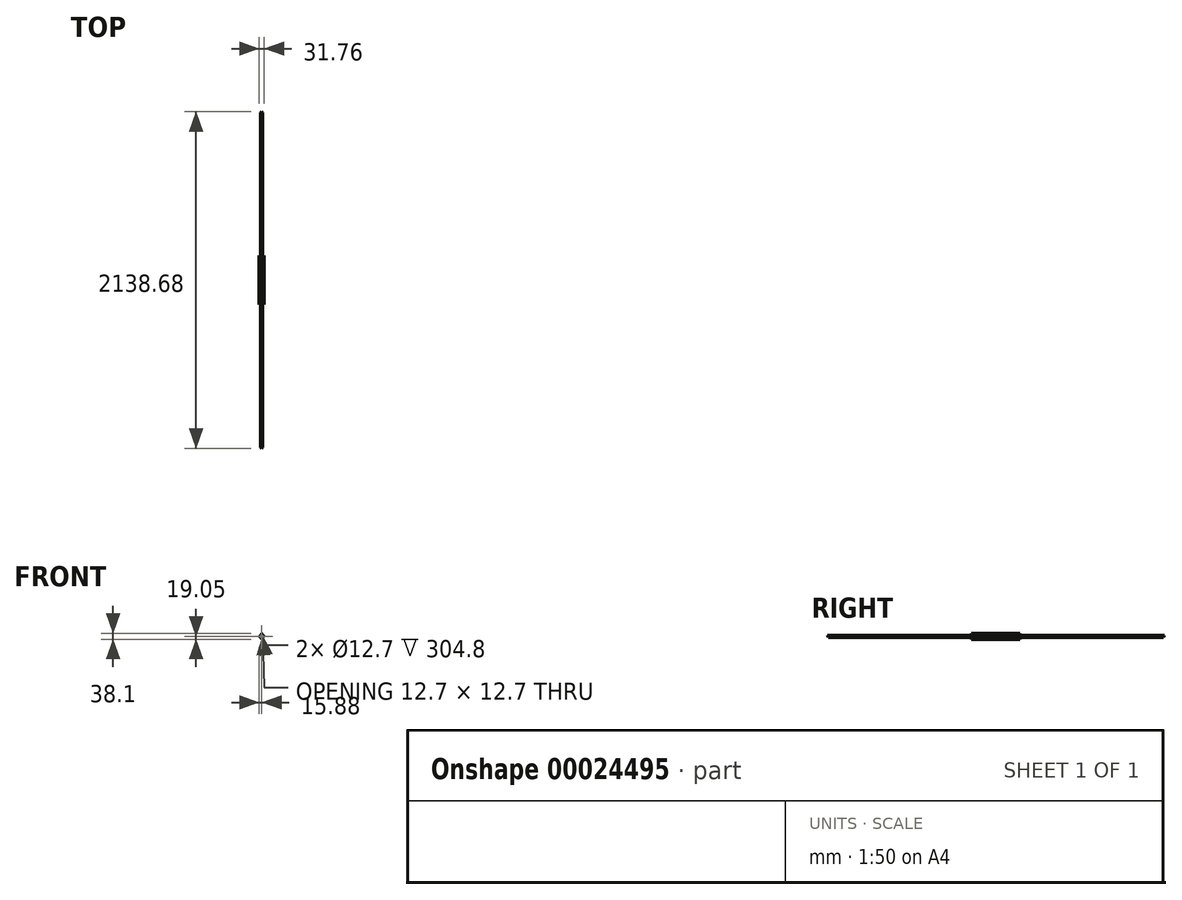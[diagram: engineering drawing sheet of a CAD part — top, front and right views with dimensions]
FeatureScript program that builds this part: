
annotation { "Feature Type Name" : "Feature", "Feature Type Description" : "" }
export const myFeature = defineFeature(function(context is Context, id is Id, definition is map)
    precondition{}
    {
        {
            var Q0;
            Q0=qCreatedBy(makeId("Right.planeOp"),FACE);
            var sketch = newSketch(context, id + "F0", { "sketchPlane" : qUnion([Q0])});
            skLineSegment(sketch, "E0.bottom", {"start": v(0, 0) * mm, "end": v(-914.4, 0) * mm});
            skLineSegment(sketch, "E0.top", {"start": v(0, 12.7) * mm, "end": v(-914.4, 12.7) * mm});
            skLineSegment(sketch, "E0.left", {"start": v(0, 0) * mm, "end": v(0, 12.7) * mm});
            skLineSegment(sketch, "E0.right", {"start": v(-914.4, 0) * mm, "end": v(-914.4, 12.7) * mm});
            skSolve(sketch);
        }
        {
            var Q0;
            Q0 = qSketchRegion(id + "F0", true);
            extrude(context, id + "F1", {"entities" : qUnion([Q0]), "depth" : 12.7 * mm});
        }
        {
            var Q0;
            Q0=makeQuery(id+"F1.opExtrude","SWEPT_FACE",FACE,{"disambiguationData":[OSD([sQuery(id+"F0.wireOp",EDGE,"E0.left")])]});
            var sketch = newSketch(context, id + "F2", { "sketchPlane" : qUnion([Q0])});
            skLineSegment(sketch, "E1", {"start": v(-12.7, 12.7) * mm, "end": v(-6.35, 0) * mm});
            skLineSegment(sketch, "E2", {"start": v(-6.35, 0) * mm, "end": v(0, 12.7) * mm});
            skSolve(sketch);
        }
        {
            var Q0;
            Q0 = qSketchRegion(id + "F2", true);
            var Q1;
            {var subQ0=sQuery(id+"F2.wireOp",EDGE,"E1");Q1=makeQuery(id+"F2.imprint","IMPRINT",FACE,{"disambiguationData":[TD([[makeQuery(id+"F2.imprint","IMPRINT",EDGE,{"derivedFrom":subQ0}),-1.0]])]});}
            var Q2;
            {var subQ0=sQuery(id+"F2.wireOp",EDGE,"E2");Q2=makeQuery(id+"F2.imprint","IMPRINT",FACE,{"disambiguationData":[TD([[makeQuery(id+"F2.imprint","IMPRINT",EDGE,{"derivedFrom":subQ0}),-1.0]])]});}
            extrude(context, id + "F3", {"entities" : qUnion([Q0, Q1, Q2]), "operationType" : NewBodyOperationType.REMOVE, "oppositeDirection" : true, "depth" : 939.8 * mm});
        }
        {
            var Q0;
            Q0=makeQuery(id+"F3.boolean.opBoolean","INTERSECT",EDGE,{"derivedFrom":[makeQuery(id+"F1.opExtrude","SWEPT_FACE",FACE,{"disambiguationData":[OSD([sQuery(id+"F0.wireOp",EDGE,"E0.right")])]}),makeQuery(id+"F3.opExtrude","SWEPT_FACE",FACE,{"disambiguationData":[OSD([sQuery(id+"F2.wireOp",EDGE,"E2")])]})]});
            var Q1;
            Q1=makeQuery(id+"F3.boolean.opBoolean","INTERSECT",EDGE,{"derivedFrom":[makeQuery(id+"F1.opExtrude","SWEPT_FACE",FACE,{"disambiguationData":[OSD([sQuery(id+"F0.wireOp",EDGE,"E0.right")])]}),makeQuery(id+"F3.opExtrude","SWEPT_FACE",FACE,{"disambiguationData":[OSD([sQuery(id+"F2.wireOp",EDGE,"E1")])]})]});
            chamfer(context, id + "F4", {"entities" : qUnion([Q0, Q1]), "width" : 5.66 * mm, "tangentPropagation" : true});
        }
        {
            var Q0;
            Q0=makeQuery(id+"F1.opExtrude","SWEPT_FACE",FACE,{"disambiguationData":[OSD([sQuery(id+"F0.wireOp",EDGE,"E0.left")])]});
            var sketch = newSketch(context, id + "F5", { "sketchPlane" : qUnion([Q0])});
            skLineSegment(sketch, "E3", {"start": v(-6.35, 0) * mm, "end": v(-6.35, -12.7) * mm});
            skLineSegment(sketch, "E4", {"start": v(-6.35, 12.7) * mm, "end": v(-6.35, 25.4) * mm});
            skLineSegment(sketch, "E5", {"start": v(-9.53, 6.35) * mm, "end": v(-22.23, 6.35) * mm});
            skLineSegment(sketch, "E6", {"start": v(-3.18, 6.35) * mm, "end": v(9.52, 6.35) * mm});
            skArc(sketch, "E7", {"start": v(-22.23, 6.35) * mm, "mid": v(-12.43, 14.33) * mm, "end": v(-6.35, 25.4) * mm});
            skArc(sketch, "E8", {"start": v(-6.35, 25.4) * mm, "mid": v(-0.27, 14.33) * mm, "end": v(9.52, 6.35) * mm});
            skArc(sketch, "E9", {"start": v(-6.35, -12.7) * mm, "mid": v(-12.43, -1.63) * mm, "end": v(-22.23, 6.35) * mm});
            skArc(sketch, "E10", {"start": v(9.52, 6.35) * mm, "mid": v(-0.27, -1.63) * mm, "end": v(-6.35, -12.7) * mm});
            skSolve(sketch);
        }
        {
            var Q0;
            Q0 = qSketchRegion(id + "F5", true);
            extrude(context, id + "F6", {"entities" : qUnion([Q0]), "depth" : 2.54 * mm});
        }
        {
            var Q0;
            Q0 = qSketchRegion(id + "F5", true);
            extrude(context, id + "F7", {"entities" : qUnion([Q0]), "depth" : 2.54 * mm});
        }
        {
            var Q0;
            Q0=makeQuery(id+"F6.opExtrude","CAP_FACE",FACE,{"disambiguationData":[OSD([sQuery(id+"F5.wireOp",EDGE,"E7"),sQuery(id+"F5.wireOp",EDGE,"E8"),sQuery(id+"F5.wireOp",EDGE,"E9"),sQuery(id+"F5.wireOp",EDGE,"E10")])],"isStart":false});
            var sketch = newSketch(context, id + "F8", { "sketchPlane" : qUnion([Q0])});
            skLineSegment(sketch, "E11", {"start": v(-22.23, 6.35) * mm, "end": v(9.52, 6.35) * mm});
            skCircle(sketch, "E12", {"center": v(-6.35, 6.35) * mm, "radius": 6.35 * mm});
            skSolve(sketch);
        }
        {
            var Q0;
            Q0=makeQuery(id+"F7.opExtrude","SWEPT_BODY",BODY,{"disambiguationData":[OSD([sQuery(id+"F5.wireOp",EDGE,"E7"),sQuery(id+"F5.wireOp",EDGE,"E8"),sQuery(id+"F5.wireOp",EDGE,"E9"),sQuery(id+"F5.wireOp",EDGE,"E10")])]});
            deleteBodies(context, id + "F9", {"entities" : qUnion([Q0])});
        }
        {
            var Q0;
            {var subQ0=sQuery(id+"F8.wireOp",EDGE,"E12");var subQ1=sQuery(id+"F8.wireOp",EDGE,"E11");var subQ2=makeQuery(id+"F8.imprint","INTERSECT",VERTEX,{"disambiguationData":[OD(0.0)],"derivedFrom":[subQ1,subQ0]});Q0=makeQuery(id+"F8.imprint","IMPRINT",FACE,{"disambiguationData":[TD([[makeQuery(id+"F8.imprint","IMPRINT",EDGE,{"disambiguationData":[TD([[subQ2,-1.0]])],"derivedFrom":subQ1}),1.0]])]});}
            var Q1;
            {var subQ0=sQuery(id+"F8.wireOp",EDGE,"E12");var subQ1=sQuery(id+"F8.wireOp",EDGE,"E11");var subQ2=makeQuery(id+"F8.imprint","INTERSECT",VERTEX,{"disambiguationData":[OD(0.0)],"derivedFrom":[subQ1,subQ0]});Q1=makeQuery(id+"F8.imprint","IMPRINT",FACE,{"disambiguationData":[TD([[makeQuery(id+"F8.imprint","IMPRINT",EDGE,{"disambiguationData":[TD([[subQ2,-1.0]])],"derivedFrom":subQ1}),-1.0]])]});}
            extrude(context, id + "F10", {"entities" : qUnion([Q0, Q1]), "operationType" : NewBodyOperationType.ADD, "depth" : 152.4 * mm});
        }
        {
            var Q0;
            Q0=makeQuery(id+"F10.opExtrude","CAP_FACE",FACE,{"disambiguationData":[OSD([sQuery(id+"F8.wireOp",EDGE,"E12")])],"isStart":false});
            cPlane(context, id + "F11", {"entities" : qUnion([Q0]), "cplaneType" : CPlaneType.OFFSET, "offset" : 0 * mm, "width" : 152.4 * mm, "height" : 152.4 * mm});
        }
        {
            var Q0;
            Q0=makeQuery(id+"F6.opExtrude","SWEPT_BODY",BODY,{"disambiguationData":[OSD([sQuery(id+"F5.wireOp",EDGE,"E7"),sQuery(id+"F5.wireOp",EDGE,"E8"),sQuery(id+"F5.wireOp",EDGE,"E9"),sQuery(id+"F5.wireOp",EDGE,"E10")])]});
            var Q1;
            Q1=makeQuery(id+"F10.opExtrude","CAP_FACE",FACE,{"disambiguationData":[OSD([sQuery(id+"F8.wireOp",EDGE,"E12")])],"isStart":false});
            mirror(context, id + "F12", {"operationType" : NewBodyOperationType.ADD, "entities" : qUnion([Q0]), "mirrorPlane" : qUnion([Q1])});
        }
        {
            var Q0;
            Q0=makeQuery(id+"F1.opExtrude","SWEPT_BODY",BODY,{"disambiguationData":[OSD([sQuery(id+"F0.wireOp",EDGE,"E0.bottom"),sQuery(id+"F0.wireOp",EDGE,"E0.top"),sQuery(id+"F0.wireOp",EDGE,"E0.left"),sQuery(id+"F0.wireOp",EDGE,"E0.right")])]});
            var Q1;
            Q1=qCreatedBy(id+"F11.planeOp",FACE);
            mirror(context, id + "F13", {"entities" : qUnion([Q0]), "mirrorPlane" : qUnion([Q1])});
        }
    });
